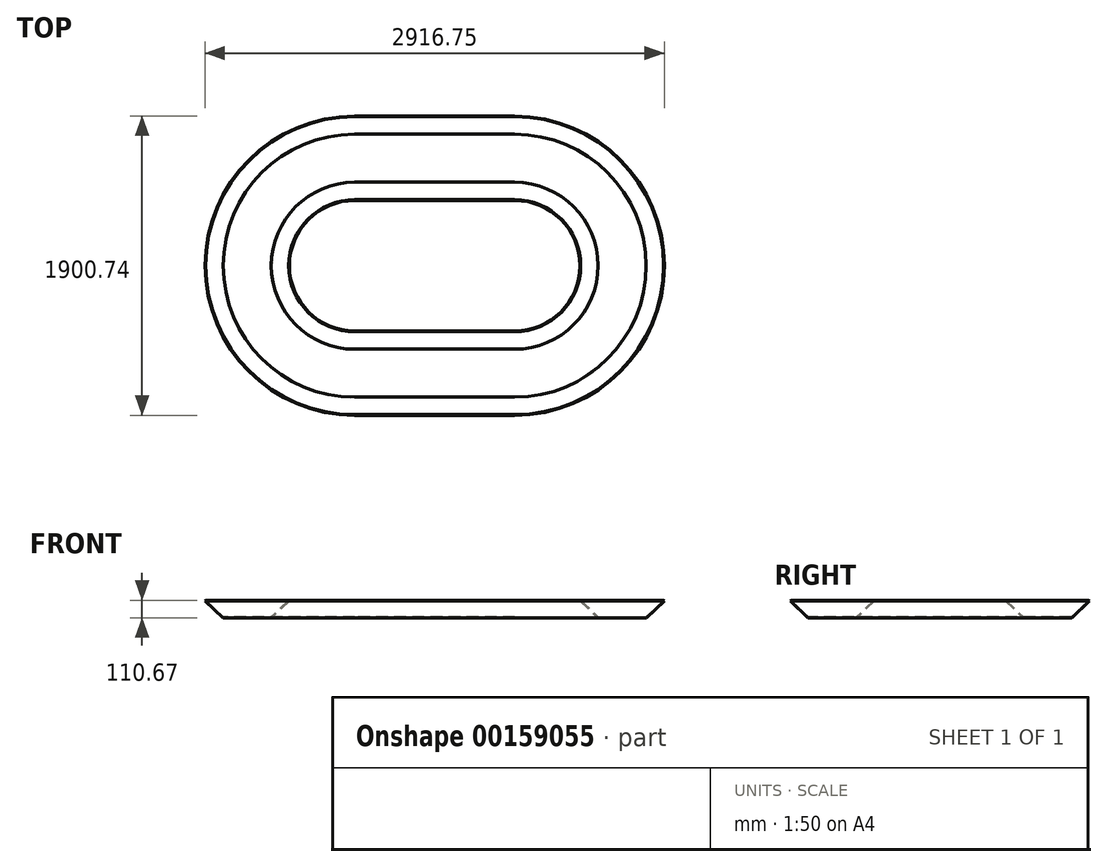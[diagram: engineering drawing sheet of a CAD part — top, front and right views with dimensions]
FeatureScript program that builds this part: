
annotation { "Feature Type Name" : "Feature", "Feature Type Description" : "" }
export const myFeature = defineFeature(function(context is Context, id is Id, definition is map)
    precondition{}
    {
        {
            var Q0;
            Q0=qCreatedBy(makeId("Right.planeOp"),FACE);
            var sketch = newSketch(context, id + "F0", { "sketchPlane" : qUnion([Q0])});
            skLineSegment(sketch, "E0", {"start": v(-146.22, 104.32) * mm, "end": v(-35.13, 0) * mm});
            skLineSegment(sketch, "E1", {"start": v(-35.13, 0) * mm, "end": v(269.67, 0) * mm});
            skLineSegment(sketch, "E2", {"start": v(117.27, 0) * mm, "end": v(117.27, 96.38) * mm, "construction": true});
            skLineSegment(sketch, "E3.MirrorCS", {"start": v(380.77, 104.32) * mm, "end": v(269.67, 0) * mm});
            skLineSegment(sketch, "E4.0", {"start": v(385.11, 99.7) * mm, "end": v(272.19, -6.35) * mm});
            skLineSegment(sketch, "E4.1", {"start": v(-37.64, -6.35) * mm, "end": v(272.19, -6.35) * mm});
            skLineSegment(sketch, "E4.2", {"start": v(-150.57, 99.7) * mm, "end": v(-37.64, -6.35) * mm});
            skLineSegment(sketch, "E5", {"start": v(-146.22, 104.32) * mm, "end": v(-150.57, 99.7) * mm});
            skLineSegment(sketch, "E6", {"start": v(380.77, 104.32) * mm, "end": v(385.11, 99.7) * mm});
            skSolve(sketch);
        }
        {
            var Q0;
            Q0=qCreatedBy(makeId("Top.planeOp"),FACE);
            var sketch = newSketch(context, id + "F1", { "sketchPlane" : qUnion([Q0])});
            skLineSegment(sketch, "E7", {"start": v(-1001.72, -565.26) * mm, "end": v(14.28, -565.26) * mm, "construction": true});
            skArc(sketch, "E8.0.startCap", {"start": v(-1001.72, -1174.86) * mm, "mid": v(-1611.32, -565.26) * mm, "end": v(-1001.72, 44.34) * mm});
            skArc(sketch, "E8.0.endCap", {"start": v(14.28, 44.34) * mm, "mid": v(623.88, -565.26) * mm, "end": v(14.28, -1174.86) * mm});
            skLineSegment(sketch, "E8.0.left", {"start": v(-1001.72, 44.34) * mm, "end": v(14.28, 44.34) * mm});
            skLineSegment(sketch, "E8.0.right", {"start": v(-1001.72, -1174.86) * mm, "end": v(14.28, -1174.86) * mm});
            skSolve(sketch);
        }
        {
            var Q0;
            Q0 = qSketchRegion(id + "F0", true);
            var Q1;
            Q1 = qConstructionFilter(qBodyType(qCreatedBy(id + "F1" ,EDGE), BodyType.WIRE), ConstructionObject.NO);
            sweep(context, id + "F2", {"profiles" : qUnion([Q0]), "path" : qUnion([Q1])});
        }
    });
